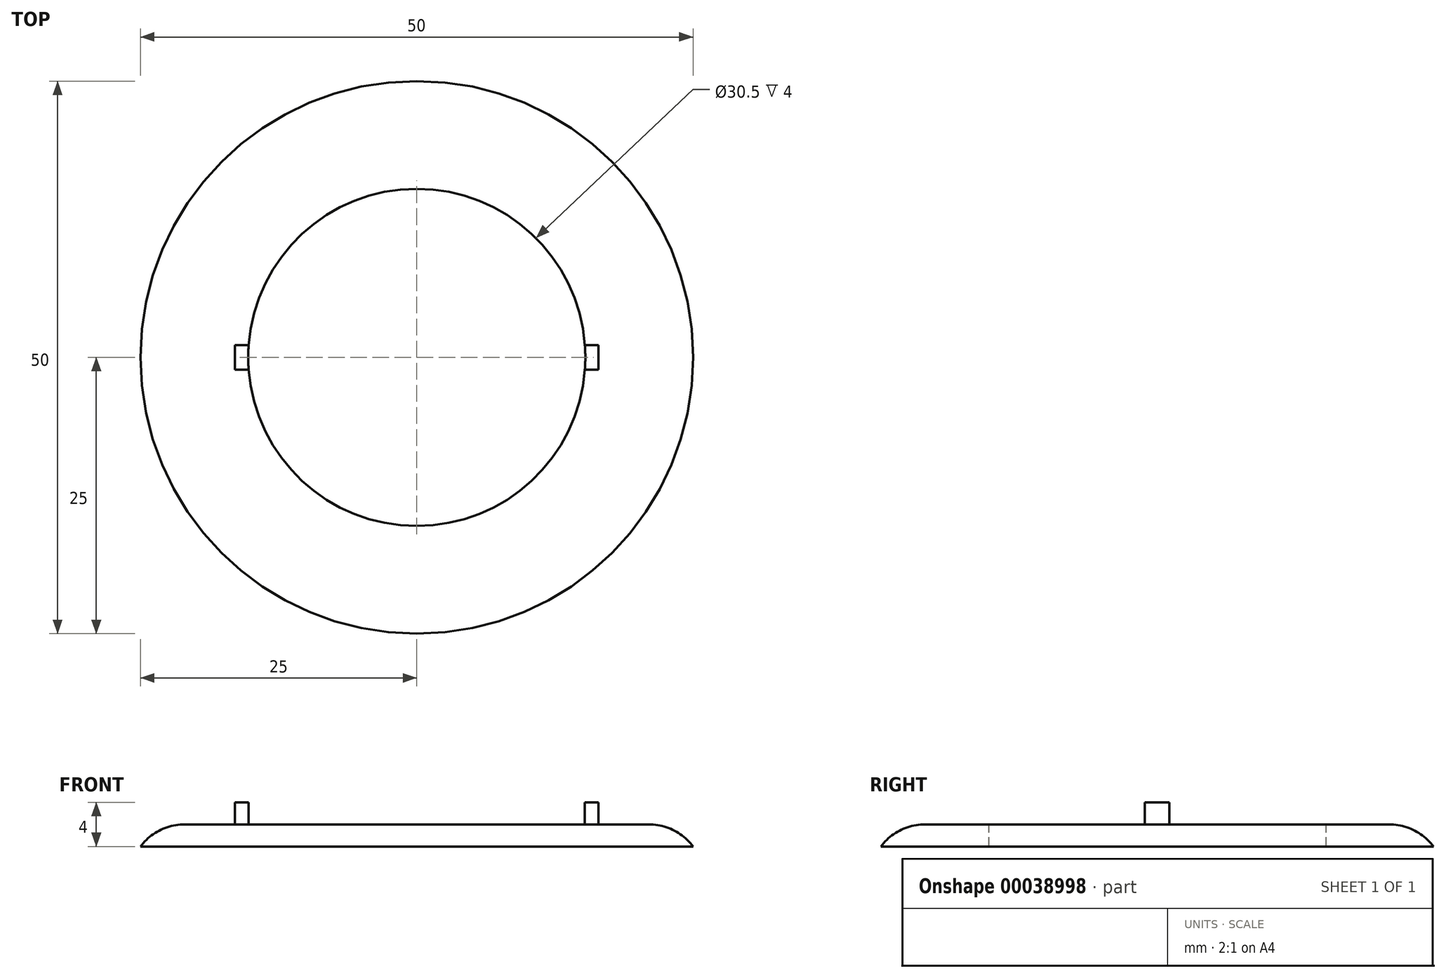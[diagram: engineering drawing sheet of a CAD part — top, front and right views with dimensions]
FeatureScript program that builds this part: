
annotation { "Feature Type Name" : "Feature", "Feature Type Description" : "" }
export const myFeature = defineFeature(function(context is Context, id is Id, definition is map)
    precondition{}
    {
        {
            var Q0;
            Q0=qCreatedBy(makeId("Top.planeOp"),FACE);
            var sketch = newSketch(context, id + "F0", { "sketchPlane" : qUnion([Q0])});
            skCircle(sketch, "E0", {"center": v(0, 0) * mm, "radius": 25 * mm});
            skCircle(sketch, "E1", {"center": v(0, 0) * mm, "radius": 15.25 * mm});
            skLineSegment(sketch, "E2.rect.bottom", {"start": v(20.84, -1.12) * mm, "end": v(-20.84, -1.12) * mm});
            skLineSegment(sketch, "E2.rect.top", {"start": v(20.84, 1.12) * mm, "end": v(-20.84, 1.12) * mm});
            skLineSegment(sketch, "E2.rect.left", {"start": v(20.84, -1.12) * mm, "end": v(20.84, 1.12) * mm, "construction": true});
            skLineSegment(sketch, "E2.rect.right", {"start": v(-20.84, -1.12) * mm, "end": v(-20.84, 1.12) * mm, "construction": true});
            skLineSegment(sketch, "E3", {"start": v(-16.45, 1.12) * mm, "end": v(-16.45, -1.12) * mm});
            skLineSegment(sketch, "E4", {"start": v(16.45, 1.12) * mm, "end": v(16.45, -1.12) * mm});
            skSolve(sketch);
        }
        {
            var Q0;
            Q0=makeQuery(id+"F0.imprint","IMPRINT",FACE,{"disambiguationData":[TD([[makeQuery(id+"F0.imprint","IMPRINT",EDGE,{"derivedFrom":sQuery(id+"F0.wireOp",EDGE,"E0")}),1.0]])]});
            var Q1;
            {var subQ0=sQuery(id+"F0.wireOp",EDGE,"E4");Q1=makeQuery(id+"F0.imprint","IMPRINT",FACE,{"disambiguationData":[TD([[makeQuery(id+"F0.imprint","IMPRINT",EDGE,{"derivedFrom":subQ0}),-1.0]])]});}
            var Q2;
            {var subQ0=sQuery(id+"F0.wireOp",EDGE,"E3");Q2=makeQuery(id+"F0.imprint","IMPRINT",FACE,{"disambiguationData":[TD([[makeQuery(id+"F0.imprint","IMPRINT",EDGE,{"derivedFrom":subQ0}),1.0]])]});}
            extrude(context, id + "F1", {"entities" : qUnion([Q0, Q1, Q2]), "depth" : 2 * mm});
        }
        {
            var Q0;
            Q0=makeQuery(id+"F1.opExtrude","CAP_EDGE",EDGE,{"disambiguationData":[OSD([sQuery(id+"F0.wireOp",EDGE,"E0")])],"isStart":false});
            fillet(context, id + "F2", {"entities" : qUnion([Q0]), "radius" : 5 * mm, "tangentPropagation" : true, "allowEdgeOverflow" : false});
        }
        {
            var Q0;
            {var subQ0=sQuery(id+"F0.wireOp",EDGE,"E4");Q0=makeQuery(id+"F0.imprint","IMPRINT",FACE,{"disambiguationData":[TD([[makeQuery(id+"F0.imprint","IMPRINT",EDGE,{"derivedFrom":subQ0}),-1.0]])]});}
            var Q1;
            {var subQ0=sQuery(id+"F0.wireOp",EDGE,"E3");Q1=makeQuery(id+"F0.imprint","IMPRINT",FACE,{"disambiguationData":[TD([[makeQuery(id+"F0.imprint","IMPRINT",EDGE,{"derivedFrom":subQ0}),1.0]])]});}
            extrude(context, id + "F3", {"entities" : qUnion([Q0, Q1]), "operationType" : NewBodyOperationType.ADD, "depth" : 4 * mm});
        }
    });
